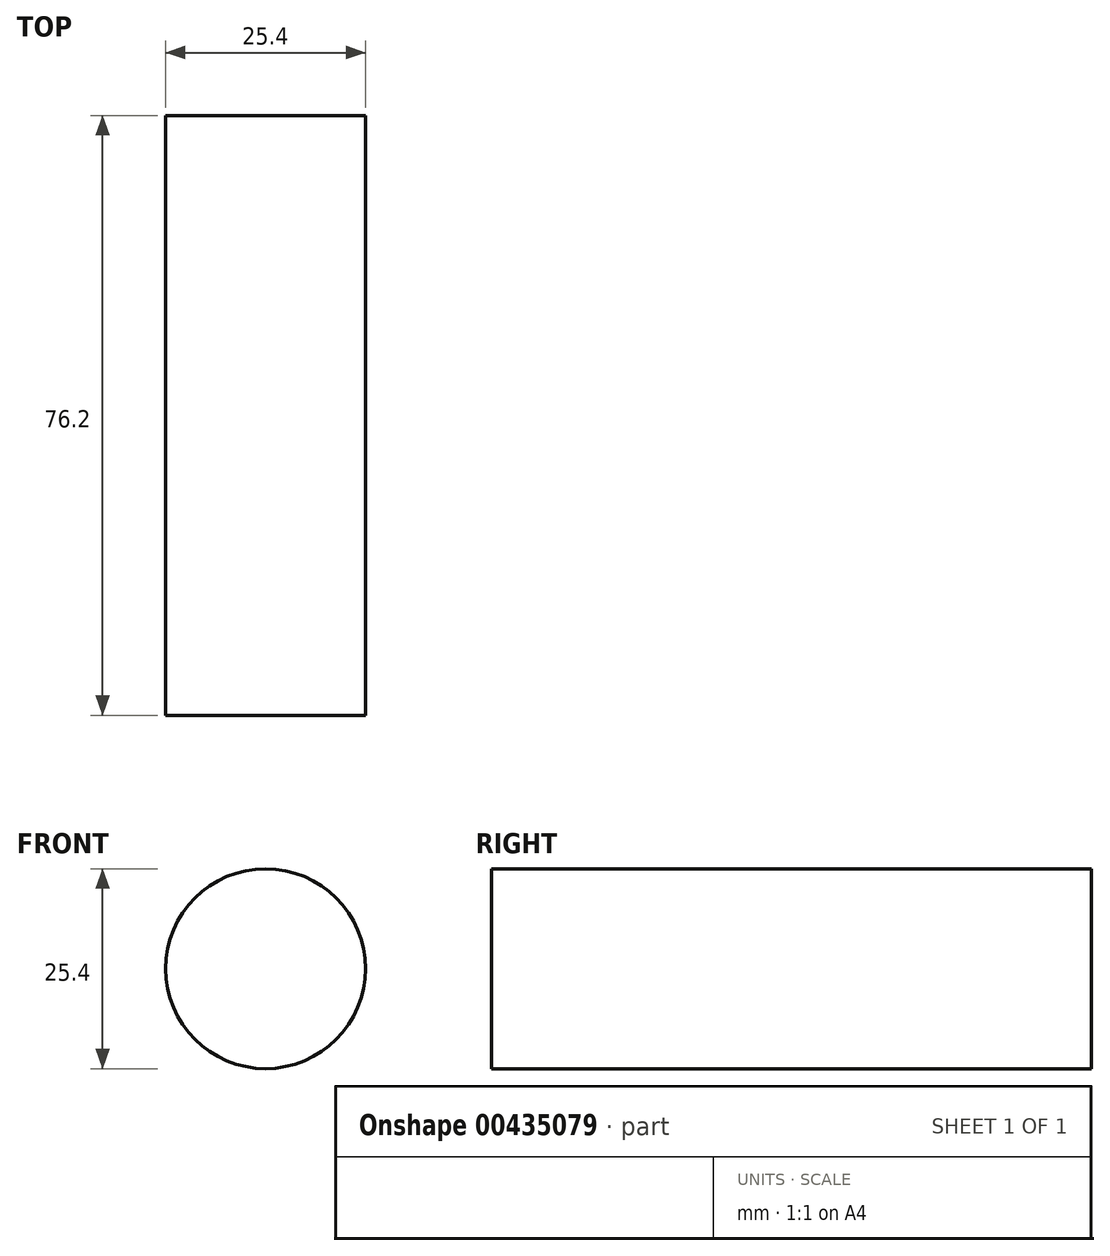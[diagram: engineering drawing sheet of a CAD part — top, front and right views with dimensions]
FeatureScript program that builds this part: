
annotation { "Feature Type Name" : "Feature", "Feature Type Description" : "" }
export const myFeature = defineFeature(function(context is Context, id is Id, definition is map)
    precondition{}
    {
        {
            var Q0;
            Q0=qCreatedBy(makeId("Front.planeOp"),FACE);
            var sketch = newSketch(context, id + "F0", { "sketchPlane" : qUnion([Q0])});
            skCircle(sketch, "E0", {"center": v(27.05, 30) * mm, "radius": 12.7 * mm});
            skSolve(sketch);
        }
        {
            var Q0;
            Q0=makeQuery(id+"F0.imprint","IMPRINT",FACE,{"disambiguationData":[TD([[makeQuery(id+"F0.imprint","IMPRINT",EDGE,{"derivedFrom":sQuery(id+"F0.wireOp",EDGE,"E0")}),1.0]])]});
            extrude(context, id + "F1", {"entities" : qUnion([Q0]), "depth" : 76.2 * mm});
        }
    });
